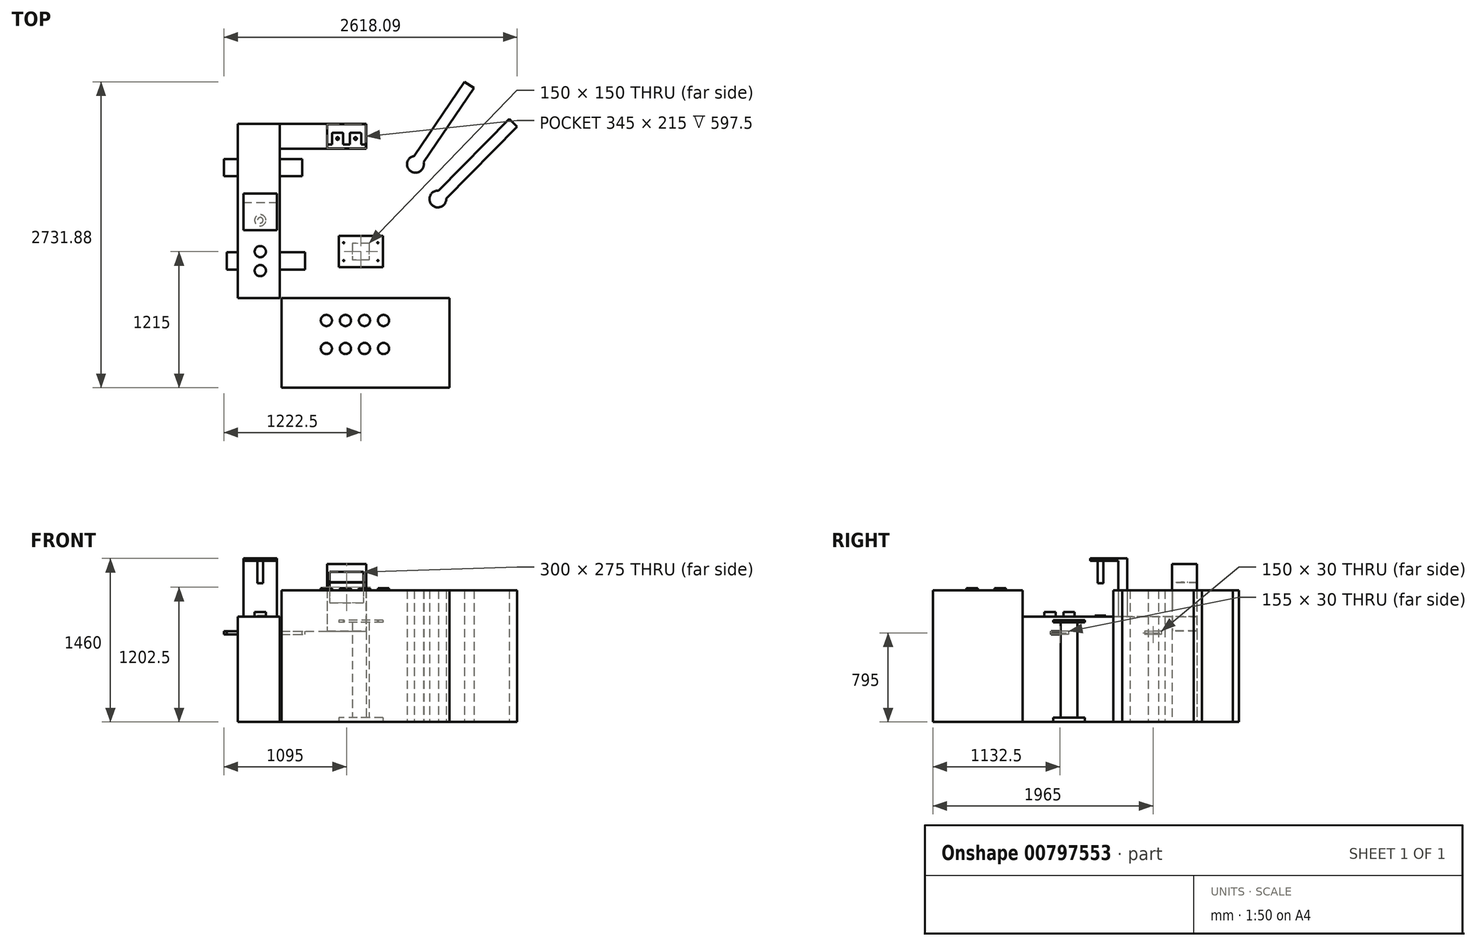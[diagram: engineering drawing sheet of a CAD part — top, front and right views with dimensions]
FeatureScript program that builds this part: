
annotation { "Feature Type Name" : "Feature", "Feature Type Description" : "" }
export const myFeature = defineFeature(function(context is Context, id is Id, definition is map)
    precondition{}
    {
        {
            var Q0;
            Q0=qCreatedBy(makeId("Top.planeOp"),FACE);
            var sketch = newSketch(context, id + "F0", { "sketchPlane" : qUnion([Q0])});
            skLineSegment(sketch, "E0.bottom", {"start": v(197.5, 140) * mm, "end": v(-197.5, 140) * mm});
            skLineSegment(sketch, "E0.top", {"start": v(197.5, -140) * mm, "end": v(-197.5, -140) * mm});
            skLineSegment(sketch, "E0.left", {"start": v(197.5, 140) * mm, "end": v(197.5, -140) * mm});
            skLineSegment(sketch, "E0.right", {"start": v(-197.5, 140) * mm, "end": v(-197.5, -140) * mm});
            skPoint(sketch, "E0.middle", {"position": v(0, 0) * mm});
            skSolve(sketch);
        }
        {
            var Q0;
            Q0 = qSketchRegion(id + "F0", true);
            extrude(context, id + "F1", {"entities" : qUnion([Q0]), "depth" : 40 * mm, "offsetDistance" : 25 * mm});
        }
        {
            var Q0;
            Q0=makeQuery(id+"F1.opExtrude","CAP_FACE",FACE,{"disambiguationData":[OSD([sQuery(id+"F0.wireOp",EDGE,"E0.bottom"),sQuery(id+"F0.wireOp",EDGE,"E0.top"),sQuery(id+"F0.wireOp",EDGE,"E0.left"),sQuery(id+"F0.wireOp",EDGE,"E0.right")])],"isStart":false});
            var sketch = newSketch(context, id + "F2", { "sketchPlane" : qUnion([Q0])});
            skLineSegment(sketch, "E1.bottom", {"start": v(75, 75) * mm, "end": v(-75, 75) * mm});
            skLineSegment(sketch, "E1.top", {"start": v(75, -75) * mm, "end": v(-75, -75) * mm});
            skLineSegment(sketch, "E1.left", {"start": v(75, 75) * mm, "end": v(75, -75) * mm});
            skLineSegment(sketch, "E1.right", {"start": v(-75, 75) * mm, "end": v(-75, -75) * mm});
            skPoint(sketch, "E1.middle", {"position": v(0, 0) * mm});
            skSolve(sketch);
        }
        {
            var Q0;
            Q0 = qSketchRegion(id + "F2", true);
            extrude(context, id + "F3", {"entities" : qUnion([Q0]), "operationType" : NewBodyOperationType.ADD, "depth" : 850 * mm, "offsetDistance" : 25 * mm});
        }
        {
            var Q0;
            Q0=makeQuery(id+"F3.opExtrude","CAP_FACE",FACE,{"disambiguationData":[OSD([sQuery(id+"F2.wireOp",EDGE,"E1.bottom"),sQuery(id+"F2.wireOp",EDGE,"E1.top"),sQuery(id+"F2.wireOp",EDGE,"E1.left"),sQuery(id+"F2.wireOp",EDGE,"E1.right")])],"isStart":false});
            var sketch = newSketch(context, id + "F4", { "sketchPlane" : qUnion([Q0])});
            skLineSegment(sketch, "E2.0", {"start": v(-197.5, 140) * mm, "end": v(-197.5, -140) * mm});
            skLineSegment(sketch, "E2.1", {"start": v(197.5, 140) * mm, "end": v(-197.5, 140) * mm});
            skLineSegment(sketch, "E2.2", {"start": v(197.5, 140) * mm, "end": v(197.5, -140) * mm});
            skLineSegment(sketch, "E2.3", {"start": v(197.5, -140) * mm, "end": v(-197.5, -140) * mm});
            skCircle(sketch, "E3", {"center": v(-152.5, 80) * mm, "radius": 5 * mm});
            skCircle(sketch, "E4", {"center": v(-152.5, -80) * mm, "radius": 5 * mm});
            skCircle(sketch, "E5", {"center": v(152.5, -80) * mm, "radius": 5 * mm});
            skCircle(sketch, "E6", {"center": v(152.5, 80) * mm, "radius": 5 * mm});
            skSolve(sketch);
        }
        {
            var Q0;
            Q0 = qSketchRegion(id + "F4", true);
            extrude(context, id + "F5", {"entities" : qUnion([Q0]), "operationType" : NewBodyOperationType.ADD, "depth" : 20 * mm, "offsetDistance" : 25 * mm});
        }
        {
            var Q0;
            Q0=qCreatedBy(makeId("Top.planeOp"),FACE);
            var sketch = newSketch(context, id + "F6", { "sketchPlane" : qUnion([Q0])});
            skLineSegment(sketch, "E7", {"start": v(47.5, 920) * mm, "end": v(47.5, 1140) * mm});
            skLineSegment(sketch, "E8", {"start": v(47.5, 1140) * mm, "end": v(-1097.5, 1140) * mm});
            skLineSegment(sketch, "E9", {"start": v(-1097.5, 1140) * mm, "end": v(-1097.5, -415) * mm});
            skLineSegment(sketch, "E10", {"start": v(-1097.5, -415) * mm, "end": v(-722.5, -415) * mm});
            skLineSegment(sketch, "E11", {"start": v(-722.5, -415) * mm, "end": v(-722.5, 920) * mm});
            skLineSegment(sketch, "E12", {"start": v(-722.5, 920) * mm, "end": v(47.5, 920) * mm});
            skSolve(sketch);
        }
        {
            var Q0;
            Q0 = qSketchRegion(id + "F6", true);
            extrude(context, id + "F7", {"entities" : qUnion([Q0]), "depth" : 810 * mm, "offsetDistance" : 25 * mm});
        }
        {
            var Q0;
            Q0=makeQuery(id+"F7.opExtrude","CAP_FACE",FACE,{"disambiguationData":[OSD([sQuery(id+"F6.wireOp",EDGE,"E7"),sQuery(id+"F6.wireOp",EDGE,"E8"),sQuery(id+"F6.wireOp",EDGE,"E9"),sQuery(id+"F6.wireOp",EDGE,"E10"),sQuery(id+"F6.wireOp",EDGE,"E11"),sQuery(id+"F6.wireOp",EDGE,"E12")])],"isStart":false});
            var sketch = newSketch(context, id + "F8", { "sketchPlane" : qUnion([Q0])});
            skLineSegment(sketch, "E13.bottom", {"start": v(47.5, 1140) * mm, "end": v(-302.5, 1140) * mm});
            skLineSegment(sketch, "E13.top", {"start": v(47.5, 920) * mm, "end": v(-302.5, 920) * mm});
            skLineSegment(sketch, "E13.left", {"start": v(47.5, 1140) * mm, "end": v(47.5, 920) * mm});
            skLineSegment(sketch, "E13.right", {"start": v(-302.5, 1140) * mm, "end": v(-302.5, 920) * mm});
            skSolve(sketch);
        }
        {
            var Q0;
            Q0 = qSketchRegion(id + "F8", true);
            extrude(context, id + "F9", {"entities" : qUnion([Q0]), "depth" : 600 * mm, "offsetDistance" : 25 * mm});
        }
        {
            var Q0;
            Q0=makeQuery(id+"F9.opExtrude","SWEPT_FACE",FACE,{"disambiguationData":[OSD([sQuery(id+"F8.wireOp",EDGE,"E13.top")])]});
            var sketch = newSketch(context, id + "F10", { "sketchPlane" : qUnion([Q0])});
            skLineSegment(sketch, "E14.bottom", {"start": v(-277.5, 1340) * mm, "end": v(22.5, 1340) * mm});
            skLineSegment(sketch, "E14.top", {"start": v(-277.5, 1065) * mm, "end": v(22.5, 1065) * mm});
            skLineSegment(sketch, "E14.left", {"start": v(-277.5, 1340) * mm, "end": v(-277.5, 1065) * mm});
            skLineSegment(sketch, "E14.right", {"start": v(22.5, 1340) * mm, "end": v(22.5, 1065) * mm});
            skSolve(sketch);
        }
        {
            var Q0;
            Q0=makeQuery(id+"F9.opExtrude","CAP_FACE",FACE,{"disambiguationData":[OSD([sQuery(id+"F8.wireOp",EDGE,"E13.bottom"),sQuery(id+"F8.wireOp",EDGE,"E13.top"),sQuery(id+"F8.wireOp",EDGE,"E13.left"),sQuery(id+"F8.wireOp",EDGE,"E13.right")])],"isStart":false});
            shell(context, id + "F11", {"entities" : qUnion([Q0]), "thickness" : 2.5 * mm});
        }
        {
            var Q0;
            Q0 = qSketchRegion(id + "F10", true);
            extrude(context, id + "F12", {"entities" : qUnion([Q0]), "operationType" : NewBodyOperationType.REMOVE, "endBound" : BoundingType.UP_TO_NEXT, "oppositeDirection" : true, "depth" : 25 * mm, "offsetDistance" : 25 * mm});
        }
        {
            var Q0;
            Q0=makeQuery(id+"F11.opShell","OFFSET_FACE",FACE,{"disambiguationData":[OSD([sQuery(id+"F8.wireOp",EDGE,"E13.bottom"),sQuery(id+"F8.wireOp",EDGE,"E13.top"),sQuery(id+"F8.wireOp",EDGE,"E13.left"),sQuery(id+"F8.wireOp",EDGE,"E13.right")])]});
            cPlane(context, id + "F13", {"entities" : qUnion([Q0]), "cplaneType" : CPlaneType.OFFSET, "offset" : 435 * mm, "width" : 150 * mm, "height" : 150 * mm});
        }
        {
            var Q0;
            Q0=qCreatedBy(id+"F13.planeOp",FACE);
            var sketch = newSketch(context, id + "F14", { "sketchPlane" : qUnion([Q0])});
            skCircle(sketch, "E15", {"center": v(-47.5, 1010) * mm, "radius": 12.5 * mm});
            skLineSegment(sketch, "E16", {"start": v(2.5, 957.5) * mm, "end": v(2.5, 1055) * mm});
            skLineSegment(sketch, "E17", {"start": v(-2.5, 1060) * mm, "end": v(-92.5, 1060) * mm});
            skLineSegment(sketch, "E18", {"start": v(-97.5, 1055) * mm, "end": v(-97.5, 957.5) * mm});
            skLineSegment(sketch, "E19.0", {"start": v(45, 1137.5) * mm, "end": v(-300, 1137.5) * mm});
            skLineSegment(sketch, "E20.0", {"start": v(45, 922.5) * mm, "end": v(45, 1137.5) * mm});
            skLineSegment(sketch, "E21.0", {"start": v(-300, 1137.5) * mm, "end": v(-300, 922.5) * mm});
            skLineSegment(sketch, "E22", {"start": v(2.5, 957.5) * mm, "end": v(45, 957.5) * mm});
            skLineSegment(sketch, "E23", {"start": v(-127.5, 1137.5) * mm, "end": v(-127.5, 932.95) * mm, "construction": true});
            skCircle(sketch, "E24.MirrorC", {"center": v(-207.5, 1010) * mm, "radius": 12.5 * mm});
            skLineSegment(sketch, "E25.MirrorCS", {"start": v(-257.5, 957.5) * mm, "end": v(-300, 957.5) * mm});
            skLineSegment(sketch, "E26.MirrorCS", {"start": v(-257.5, 957.5) * mm, "end": v(-257.5, 1055) * mm});
            skLineSegment(sketch, "E27.MirrorCS", {"start": v(-157.5, 1055) * mm, "end": v(-157.5, 957.5) * mm});
            skLineSegment(sketch, "E28.MirrorCS", {"start": v(-252.5, 1060) * mm, "end": v(-162.5, 1060) * mm});
            skLineSegment(sketch, "E29", {"start": v(-157.5, 957.5) * mm, "end": v(-97.5, 957.5) * mm});
            skPoint(sketch, "E30.visualSharp", {"position": v(-257.5, 1060) * mm});
            skArc(sketch, "E30.filletArc", {"start": v(-252.5, 1060) * mm, "mid": v(-256.04, 1058.54) * mm, "end": v(-257.5, 1055) * mm});
            skPoint(sketch, "E31.visualSharp", {"position": v(-157.5, 1060) * mm});
            skArc(sketch, "E31.filletArc", {"start": v(-157.5, 1055) * mm, "mid": v(-158.96, 1058.54) * mm, "end": v(-162.5, 1060) * mm});
            skPoint(sketch, "E32.visualSharp", {"position": v(-97.5, 1060) * mm});
            skArc(sketch, "E32.filletArc", {"start": v(-92.5, 1060) * mm, "mid": v(-96.04, 1058.54) * mm, "end": v(-97.5, 1055) * mm});
            skPoint(sketch, "E33.visualSharp", {"position": v(2.5, 1060) * mm});
            skArc(sketch, "E33.filletArc", {"start": v(2.5, 1055) * mm, "mid": v(1.04, 1058.54) * mm, "end": v(-2.5, 1060) * mm});
            skSolve(sketch);
        }
        {
            var Q0;
            Q0 = qSketchRegion(id + "F14", true);
            extrude(context, id + "F15", {"entities" : qUnion([Q0]), "oppositeDirection" : true, "depth" : 2 * mm, "offsetDistance" : 25 * mm});
        }
        {
            var Q0;
            Q0=qCreatedBy(makeId("Top.planeOp"),FACE);
            var sketch = newSketch(context, id + "F16", { "sketchPlane" : qUnion([Q0])});
            skCircle(sketch, "E34", {"center": v(487.5, 780) * mm, "radius": 75 * mm});
            skCircle(sketch, "E35", {"center": v(687.5, 470) * mm, "radius": 75 * mm});
            skLineSegment(sketch, "E36", {"start": v(477.42, 854.32) * mm, "end": v(925.76, 1516.88) * mm});
            skLineSegment(sketch, "E37", {"start": v(925.76, 1516.88) * mm, "end": v(1008.58, 1460.84) * mm});
            skLineSegment(sketch, "E38", {"start": v(1008.58, 1460.84) * mm, "end": v(560.24, 798.28) * mm});
            skLineSegment(sketch, "E39", {"start": v(691.3, 544.9) * mm, "end": v(1324.53, 1184.45) * mm});
            skLineSegment(sketch, "E40", {"start": v(1324.53, 1184.45) * mm, "end": v(1395.6, 1114.1) * mm});
            skLineSegment(sketch, "E41", {"start": v(1395.6, 1114.1) * mm, "end": v(762.36, 474.54) * mm});
            skSolve(sketch);
        }
        {
            var Q0;
            {var subQ0=sQuery(id+"F16.wireOp",EDGE,"E34");var subQ1=makeQuery(id+"F16.imprint","INTERSECT",VERTEX,{"derivedFrom":[subQ0,sQuery(id+"F16.wireOp",EDGE,"E36")]});Q0=makeQuery(id+"F16.imprint","IMPRINT",FACE,{"disambiguationData":[TD([[makeQuery(id+"F16.imprint","IMPRINT",EDGE,{"disambiguationData":[TD([[subQ1,1.0]])],"derivedFrom":subQ0}),1.0]])]});}
            var Q1;
            {var subQ0=sQuery(id+"F16.wireOp",EDGE,"E36");Q1=makeQuery(id+"F16.imprint","IMPRINT",FACE,{"disambiguationData":[TD([[makeQuery(id+"F16.imprint","IMPRINT",EDGE,{"derivedFrom":subQ0}),-1.0]])]});}
            extrude(context, id + "F17", {"entities" : qUnion([Q0, Q1]), "depth" : 1175 * mm, "offsetDistance" : 25 * mm});
        }
        {
            var Q0;
            {var subQ0=sQuery(id+"F16.wireOp",EDGE,"E35");var subQ1=makeQuery(id+"F16.imprint","INTERSECT",VERTEX,{"derivedFrom":[subQ0,sQuery(id+"F16.wireOp",EDGE,"E39")]});Q0=makeQuery(id+"F16.imprint","IMPRINT",FACE,{"disambiguationData":[TD([[makeQuery(id+"F16.imprint","IMPRINT",EDGE,{"disambiguationData":[TD([[subQ1,1.0]])],"derivedFrom":subQ0}),1.0]])]});}
            var Q1;
            {var subQ0=sQuery(id+"F16.wireOp",EDGE,"E39");Q1=makeQuery(id+"F16.imprint","IMPRINT",FACE,{"disambiguationData":[TD([[makeQuery(id+"F16.imprint","IMPRINT",EDGE,{"derivedFrom":subQ0}),-1.0]])]});}
            extrude(context, id + "F18", {"entities" : qUnion([Q0, Q1]), "depth" : 1175 * mm, "offsetDistance" : 25 * mm});
        }
        {
            var Q0;
            Q0=makeQuery(id+"F7.opExtrude","CAP_FACE",FACE,{"disambiguationData":[OSD([sQuery(id+"F6.wireOp",EDGE,"E7"),sQuery(id+"F6.wireOp",EDGE,"E8"),sQuery(id+"F6.wireOp",EDGE,"E9"),sQuery(id+"F6.wireOp",EDGE,"E10"),sQuery(id+"F6.wireOp",EDGE,"E11"),sQuery(id+"F6.wireOp",EDGE,"E12")])],"isStart":false});
            var sketch = newSketch(context, id + "F19", { "sketchPlane" : qUnion([Q0])});
            skLineSegment(sketch, "E42.bottom", {"start": v(-1222.5, 825) * mm, "end": v(-522.5, 825) * mm});
            skLineSegment(sketch, "E42.top", {"start": v(-1222.5, 675) * mm, "end": v(-522.5, 675) * mm});
            skLineSegment(sketch, "E42.left", {"start": v(-1222.5, 825) * mm, "end": v(-1222.5, 675) * mm});
            skLineSegment(sketch, "E42.right", {"start": v(-522.5, 825) * mm, "end": v(-522.5, 675) * mm});
            skLineSegment(sketch, "E43.bottom", {"start": v(-1197.5, -5) * mm, "end": v(-497.5, -5) * mm});
            skLineSegment(sketch, "E43.top", {"start": v(-1197.5, -160) * mm, "end": v(-497.5, -160) * mm});
            skLineSegment(sketch, "E43.left", {"start": v(-1197.5, -5) * mm, "end": v(-1197.5, -160) * mm});
            skLineSegment(sketch, "E43.right", {"start": v(-497.5, -5) * mm, "end": v(-497.5, -160) * mm});
            skSolve(sketch);
        }
        {
            var Q0;
            Q0 = qSketchRegion(id + "F19", true);
            extrude(context, id + "F20", {"entities" : qUnion([Q0]), "operationType" : NewBodyOperationType.ADD, "oppositeDirection" : true, "depth" : 30 * mm, "offsetDistance" : 25 * mm});
        }
        {
            var Q0;
            Q0=makeQuery(id+"F20.boolean.opBoolean","MERGE",FACE,{"derivedFrom":[makeQuery(id+"F7.opExtrude","CAP_FACE",FACE,{"disambiguationData":[OSD([sQuery(id+"F6.wireOp",EDGE,"E7"),sQuery(id+"F6.wireOp",EDGE,"E8"),sQuery(id+"F6.wireOp",EDGE,"E9"),sQuery(id+"F6.wireOp",EDGE,"E10"),sQuery(id+"F6.wireOp",EDGE,"E11"),sQuery(id+"F6.wireOp",EDGE,"E12")])],"isStart":false}),makeQuery(id+"F20.opExtrude","CAP_FACE",FACE,{"disambiguationData":[OSD([sQuery(id+"F19.wireOp",EDGE,"E42.bottom"),sQuery(id+"F19.wireOp",EDGE,"E42.top"),sQuery(id+"F19.wireOp",EDGE,"E42.left"),sQuery(id+"F19.wireOp",EDGE,"E42.right")])],"isStart":true}),makeQuery(id+"F20.opExtrude","CAP_FACE",FACE,{"disambiguationData":[OSD([sQuery(id+"F19.wireOp",EDGE,"E43.bottom"),sQuery(id+"F19.wireOp",EDGE,"E43.top"),sQuery(id+"F19.wireOp",EDGE,"E43.left"),sQuery(id+"F19.wireOp",EDGE,"E43.right")])],"isStart":true})]});
            var sketch = newSketch(context, id + "F21", { "sketchPlane" : qUnion([Q0])});
            skLineSegment(sketch, "E44.0", {"start": v(-1097.5, 1140) * mm, "end": v(-1097.5, 675) * mm});
            skLineSegment(sketch, "E44.1", {"start": v(-1097.5, 675) * mm, "end": v(-1097.5, -160) * mm});
            skLineSegment(sketch, "E44.2", {"start": v(-1097.5, -160) * mm, "end": v(-1097.5, -415) * mm});
            skLineSegment(sketch, "E44.3", {"start": v(-722.5, -415) * mm, "end": v(-722.5, -160) * mm});
            skLineSegment(sketch, "E44.4", {"start": v(-722.5, -160) * mm, "end": v(-722.5, 675) * mm});
            skLineSegment(sketch, "E44.5", {"start": v(-722.5, 675) * mm, "end": v(-722.5, 1140) * mm});
            skLineSegment(sketch, "E44.6", {"start": v(-722.5, 1140) * mm, "end": v(-1097.5, 1140) * mm});
            skLineSegment(sketch, "E44.7", {"start": v(-1097.5, -415) * mm, "end": v(-722.5, -415) * mm});
            skPoint(sketch, "E45.orphan", {"position": v(-1097.5, 825) * mm});
            skPoint(sketch, "E46.orphan", {"position": v(-1097.5, -5) * mm});
            skPoint(sketch, "E47.orphan", {"position": v(-722.5, -5) * mm});
            skPoint(sketch, "E48.orphan", {"position": v(-722.5, 825) * mm});
            skPoint(sketch, "E49.orphan", {"position": v(-722.5, 920) * mm});
            skPoint(sketch, "E50.orphan", {"position": v(47.5, 1140) * mm});
            skSolve(sketch);
        }
        {
            var Q0;
            Q0 = qSketchRegion(id + "F21", true);
            extrude(context, id + "F22", {"entities" : qUnion([Q0]), "operationType" : NewBodyOperationType.ADD, "depth" : 130 * mm, "offsetDistance" : 25 * mm});
        }
        {
            var Q0;
            Q0=makeQuery(id+"F22.opExtrude","CAP_FACE",FACE,{"disambiguationData":[OSD([sQuery(id+"F21.wireOp",EDGE,"E44.0"),sQuery(id+"F21.wireOp",EDGE,"E44.1"),sQuery(id+"F21.wireOp",EDGE,"E44.2"),sQuery(id+"F21.wireOp",EDGE,"E44.3"),sQuery(id+"F21.wireOp",EDGE,"E44.4"),sQuery(id+"F21.wireOp",EDGE,"E44.5"),sQuery(id+"F21.wireOp",EDGE,"E44.6"),sQuery(id+"F21.wireOp",EDGE,"E44.7")])],"isStart":false});
            var sketch = newSketch(context, id + "F23", { "sketchPlane" : qUnion([Q0])});
            skCircle(sketch, "E51", {"center": v(-897.5, 280) * mm, "radius": 50 * mm});
            skCircle(sketch, "E52", {"center": v(-897.5, 0) * mm, "radius": 50 * mm});
            skCircle(sketch, "E53", {"center": v(-897.5, -170) * mm, "radius": 50 * mm});
            skLineSegment(sketch, "E54.bottom", {"start": v(-1047.5, 520) * mm, "end": v(-747.5, 520) * mm});
            skLineSegment(sketch, "E54.top", {"start": v(-1047.5, 440) * mm, "end": v(-747.5, 440) * mm});
            skLineSegment(sketch, "E54.left", {"start": v(-1047.5, 520) * mm, "end": v(-1047.5, 440) * mm});
            skLineSegment(sketch, "E54.right", {"start": v(-747.5, 520) * mm, "end": v(-747.5, 440) * mm});
            skSolve(sketch);
        }
        {
            var Q0;
            Q0=makeQuery(id+"F23.imprint","IMPRINT",FACE,{"disambiguationData":[TD([[makeQuery(id+"F23.imprint","IMPRINT",EDGE,{"derivedFrom":sQuery(id+"F23.wireOp",EDGE,"E51")}),1.0]])]});
            extrude(context, id + "F24", {"entities" : qUnion([Q0]), "operationType" : NewBodyOperationType.ADD, "depth" : 10 * mm, "offsetDistance" : 25 * mm});
        }
        {
            var Q0;
            Q0=makeQuery(id+"F23.imprint","IMPRINT",FACE,{"disambiguationData":[TD([[makeQuery(id+"F23.imprint","IMPRINT",EDGE,{"derivedFrom":sQuery(id+"F23.wireOp",EDGE,"E54.bottom")}),-1.0]])]});
            extrude(context, id + "F25", {"entities" : qUnion([Q0]), "operationType" : NewBodyOperationType.ADD, "depth" : 500 * mm, "offsetDistance" : 25 * mm});
        }
        {
            var Q0;
            Q0=makeQuery(id+"F25.opExtrude","CAP_FACE",FACE,{"disambiguationData":[OSD([sQuery(id+"F23.wireOp",EDGE,"E54.bottom"),sQuery(id+"F23.wireOp",EDGE,"E54.top"),sQuery(id+"F23.wireOp",EDGE,"E54.left"),sQuery(id+"F23.wireOp",EDGE,"E54.right")])],"isStart":false});
            var sketch = newSketch(context, id + "F26", { "sketchPlane" : qUnion([Q0])});
            skLineSegment(sketch, "E55.bottom", {"start": v(-1047.5, 520) * mm, "end": v(-747.5, 520) * mm});
            skLineSegment(sketch, "E55.top", {"start": v(-1047.5, 190) * mm, "end": v(-747.5, 190) * mm});
            skLineSegment(sketch, "E55.left", {"start": v(-1047.5, 520) * mm, "end": v(-1047.5, 190) * mm});
            skLineSegment(sketch, "E55.right", {"start": v(-747.5, 520) * mm, "end": v(-747.5, 190) * mm});
            skCircle(sketch, "E56.0", {"center": v(-897.5, 280) * mm, "radius": 50 * mm, "construction": true});
            skCircle(sketch, "E57", {"center": v(-897.5, 280) * mm, "radius": 25 * mm});
            skSolve(sketch);
        }
        {
            var Q0;
            Q0 = qSketchRegion(id + "F26", true);
            var Q1;
            Q1=makeQuery(id+"F26.imprint","IMPRINT",FACE,{"disambiguationData":[TD([[makeQuery(id+"F26.imprint","IMPRINT",EDGE,{"derivedFrom":sQuery(id+"F26.wireOp",EDGE,"E57")}),1.0]])]});
            extrude(context, id + "F27", {"entities" : qUnion([Q0, Q1]), "operationType" : NewBodyOperationType.ADD, "depth" : 20 * mm, "offsetDistance" : 25 * mm});
        }
        {
            var Q0;
            Q0=makeQuery(id+"F26.imprint","IMPRINT",FACE,{"disambiguationData":[TD([[makeQuery(id+"F26.imprint","IMPRINT",EDGE,{"derivedFrom":sQuery(id+"F26.wireOp",EDGE,"E57")}),1.0]])]});
            extrude(context, id + "F28", {"entities" : qUnion([Q0]), "operationType" : NewBodyOperationType.ADD, "oppositeDirection" : true, "depth" : 200 * mm, "offsetDistance" : 25 * mm});
        }
        {
            var Q0;
            Q0=makeQuery(id+"F23.imprint","IMPRINT",FACE,{"disambiguationData":[TD([[makeQuery(id+"F23.imprint","IMPRINT",EDGE,{"derivedFrom":sQuery(id+"F23.wireOp",EDGE,"E52")}),1.0]])]});
            var Q1;
            Q1=makeQuery(id+"F23.imprint","IMPRINT",FACE,{"disambiguationData":[TD([[makeQuery(id+"F23.imprint","IMPRINT",EDGE,{"derivedFrom":sQuery(id+"F23.wireOp",EDGE,"E53")}),1.0]])]});
            extrude(context, id + "F29", {"entities" : qUnion([Q0, Q1]), "operationType" : NewBodyOperationType.ADD, "depth" : 40 * mm, "offsetDistance" : 25 * mm});
        }
        {
            var Q0;
            Q0=qCreatedBy(makeId("Top.planeOp"),FACE);
            var sketch = newSketch(context, id + "F30", { "sketchPlane" : qUnion([Q0])});
            skLineSegment(sketch, "E58.bottom", {"start": v(-707.5, -415) * mm, "end": v(792.5, -415) * mm});
            skLineSegment(sketch, "E58.top", {"start": v(-707.5, -1215) * mm, "end": v(792.5, -1215) * mm});
            skLineSegment(sketch, "E58.left", {"start": v(-707.5, -415) * mm, "end": v(-707.5, -1215) * mm});
            skLineSegment(sketch, "E58.right", {"start": v(792.5, -415) * mm, "end": v(792.5, -1215) * mm});
            skSolve(sketch);
        }
        {
            var Q0;
            Q0 = qSketchRegion(id + "F30", true);
            extrude(context, id + "F31", {"entities" : qUnion([Q0]), "depth" : 1175 * mm, "offsetDistance" : 25 * mm});
        }
        {
            var Q0;
            Q0=makeQuery(id+"F31.opExtrude","CAP_FACE",FACE,{"disambiguationData":[OSD([sQuery(id+"F30.wireOp",EDGE,"E58.bottom"),sQuery(id+"F30.wireOp",EDGE,"E58.top"),sQuery(id+"F30.wireOp",EDGE,"E58.left"),sQuery(id+"F30.wireOp",EDGE,"E58.right")])],"isStart":false});
            var sketch = newSketch(context, id + "F32", { "sketchPlane" : qUnion([Q0])});
            skCircle(sketch, "E59", {"center": v(-307.5, -615) * mm, "radius": 50 * mm});
            skCircle(sketch, "E60.0.1.0", {"center": v(-307.5, -865) * mm, "radius": 50 * mm});
            skCircle(sketch, "E60.1.0.0", {"center": v(-137.5, -615) * mm, "radius": 50 * mm});
            skCircle(sketch, "E60.1.1.0", {"center": v(-137.5, -865) * mm, "radius": 50 * mm});
            skCircle(sketch, "E60.2.0.0", {"center": v(32.5, -615) * mm, "radius": 50 * mm});
            skCircle(sketch, "E60.2.1.0", {"center": v(32.5, -865) * mm, "radius": 50 * mm});
            skCircle(sketch, "E60.3.0.0", {"center": v(202.5, -615) * mm, "radius": 50 * mm});
            skCircle(sketch, "E60.3.1.0", {"center": v(202.5, -865) * mm, "radius": 50 * mm});
            skLineSegment(sketch, "E60.direction1", {"start": v(-307.5, -615) * mm, "end": v(-137.5, -615) * mm, "construction": true});
            skLineSegment(sketch, "E60.direction2", {"start": v(-307.5, -615) * mm, "end": v(-307.5, -865) * mm, "construction": true});
            skSolve(sketch);
        }
        {
            var Q0;
            Q0 = qSketchRegion(id + "F32", true);
            extrude(context, id + "F33", {"entities" : qUnion([Q0]), "operationType" : NewBodyOperationType.ADD, "depth" : 20 * mm, "offsetDistance" : 25 * mm});
        }
    });
